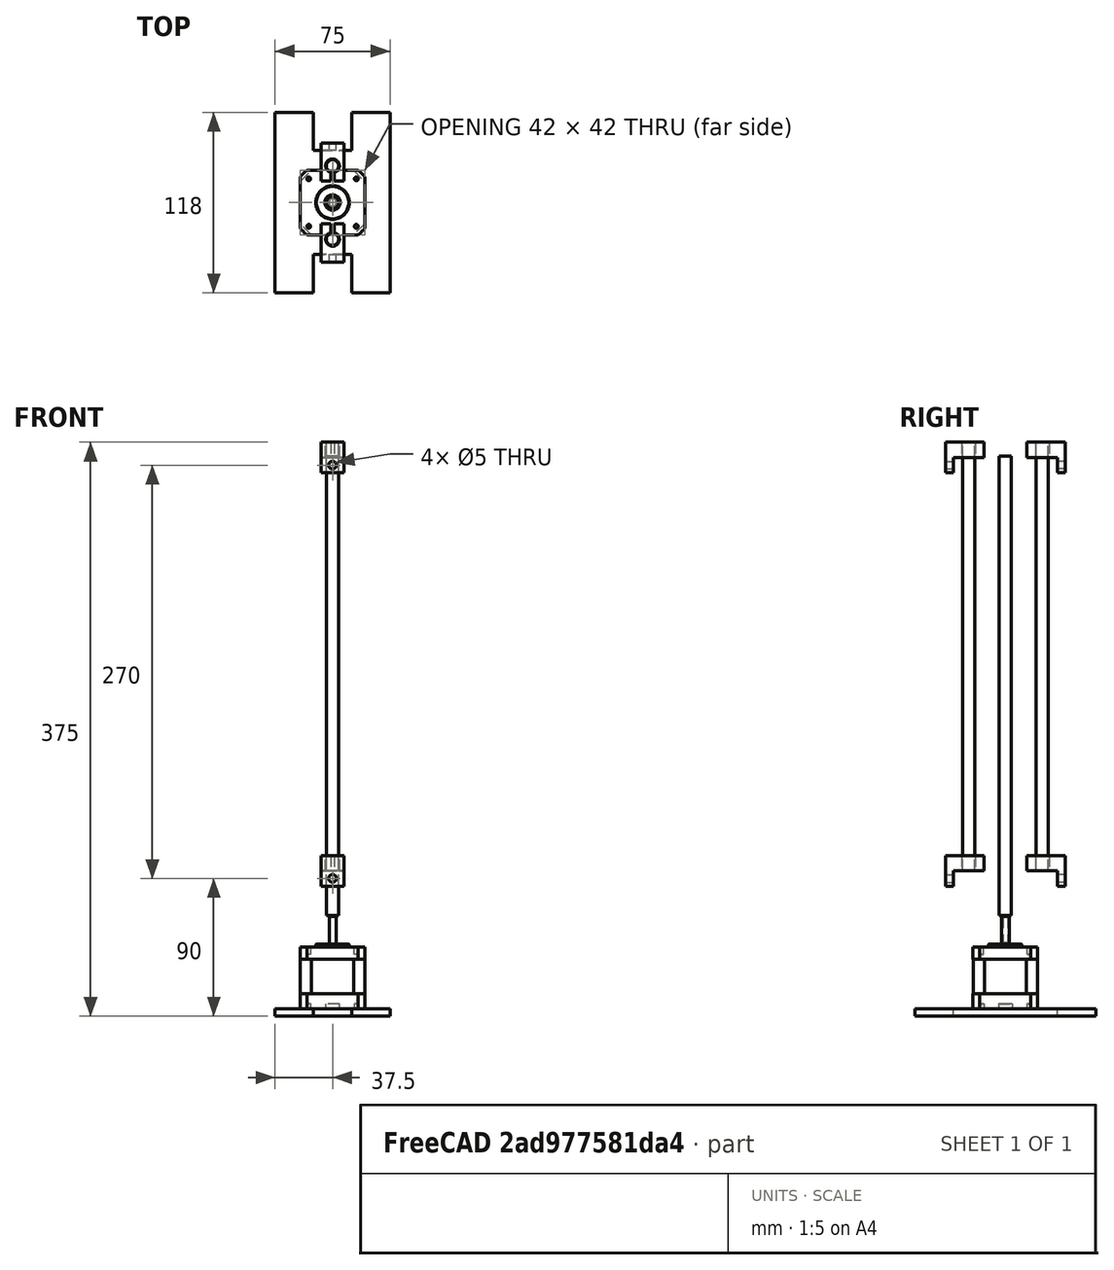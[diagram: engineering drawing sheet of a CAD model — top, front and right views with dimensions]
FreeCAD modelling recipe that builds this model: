
FCSTD DOCUMENT  (FreeCAD 0.16R5231 (Git))
Label: zAxis
License: All rights reserved
LicenseURL: http://en.wikipedia.org/wiki/All_rights_reserved
objects: Part::FeaturePython×7, Part::Cylinder×3
note: 10 computed .brp shape members not serialized (recipe doc carries the construction recipe); baked Part::Feature solids carry a one-line shape summary decoded from their .brp

FEATURE [Part::Cylinder] Cylinder  label="Welle1"
  Angle = 360
  Height = 280
  Placement = pos=(-3.5,76,115) rot=(0,0,1;0rad)
  Radius = 4
FEATURE [Part::FeaturePython] BuildPlatformMountingP2_01  # a2plus imported part (geometry in sourceFile) (typed FeaturePython)
  Placement = pos=(-3.5,76,375) rot=(0,0,1;0rad)
  fixedPosition = false
  sourceFile = <path>
  timeLastImport = 1.43833e+09
FEATURE [Part::Cylinder] Cylinder002  label="Spindel"
  Angle = 360
  Height = 300
  Placement = pos=(-3.5,100,86) rot=(0,0,1;0rad)
  Radius = 4
FEATURE [Part::Cylinder] Cylinder001  label="Welle2"
  Angle = 360
  Height = 280
  Placement = pos=(-3.5,124,115) rot=(0,0,1;0rad)
  Radius = 4
FEATURE [Part::FeaturePython] BuildPlatformMountingP2_002  # a2plus imported part (geometry in sourceFile) (typed FeaturePython)
  Placement = pos=(-3.5,76,105) rot=(0,0,1;0rad)
  fixedPosition = false
  sourceFile = <path>
  timeLastImport = 1.43833e+09
FEATURE [Part::FeaturePython] BuildPlatformMountingP2_003  # a2plus imported part (geometry in sourceFile) (typed FeaturePython)
  Placement = pos=(-3.5,124,375) rot=(0,0,1;3.14159rad)
  fixedPosition = false
  sourceFile = <path>
  timeLastImport = 1.43833e+09
FEATURE [Part::FeaturePython] BuildPlatformMountingP2_004  # a2plus imported part (geometry in sourceFile) (typed FeaturePython)
  Placement = pos=(-3.5,124,105) rot=(0,0,1;3.14159rad)
  fixedPosition = false
  sourceFile = <path>
  timeLastImport = 1.43833e+09
FEATURE [Part::FeaturePython] NEMA_17_Stepper_Motor_40mm_01  # a2plus imported part (geometry in sourceFile) (typed FeaturePython)
  Placement = pos=(-3.5,100,25) rot=(0,0,1;0rad)
  fixedPosition = false
  sourceFile = <path>
  timeLastImport = 1.43833e+09
FEATURE [Part::FeaturePython] StepperBase_01  # a2plus imported part (geometry in sourceFile) (typed FeaturePython)
  Placement = pos=(-41,41,20) rot=(0,0,1;0rad)
  fixedPosition = false
  sourceFile = <path>
  timeLastImport = 1.43888e+09
FEATURE [Part::FeaturePython] muxedAssembly  # WARN: FeaturePython — macro-defined, semantics opaque (R4)
  type = muxedAssembly
note: 6 file-system paths scrubbed to <path> (originals preserved in the JSON sidecar)
